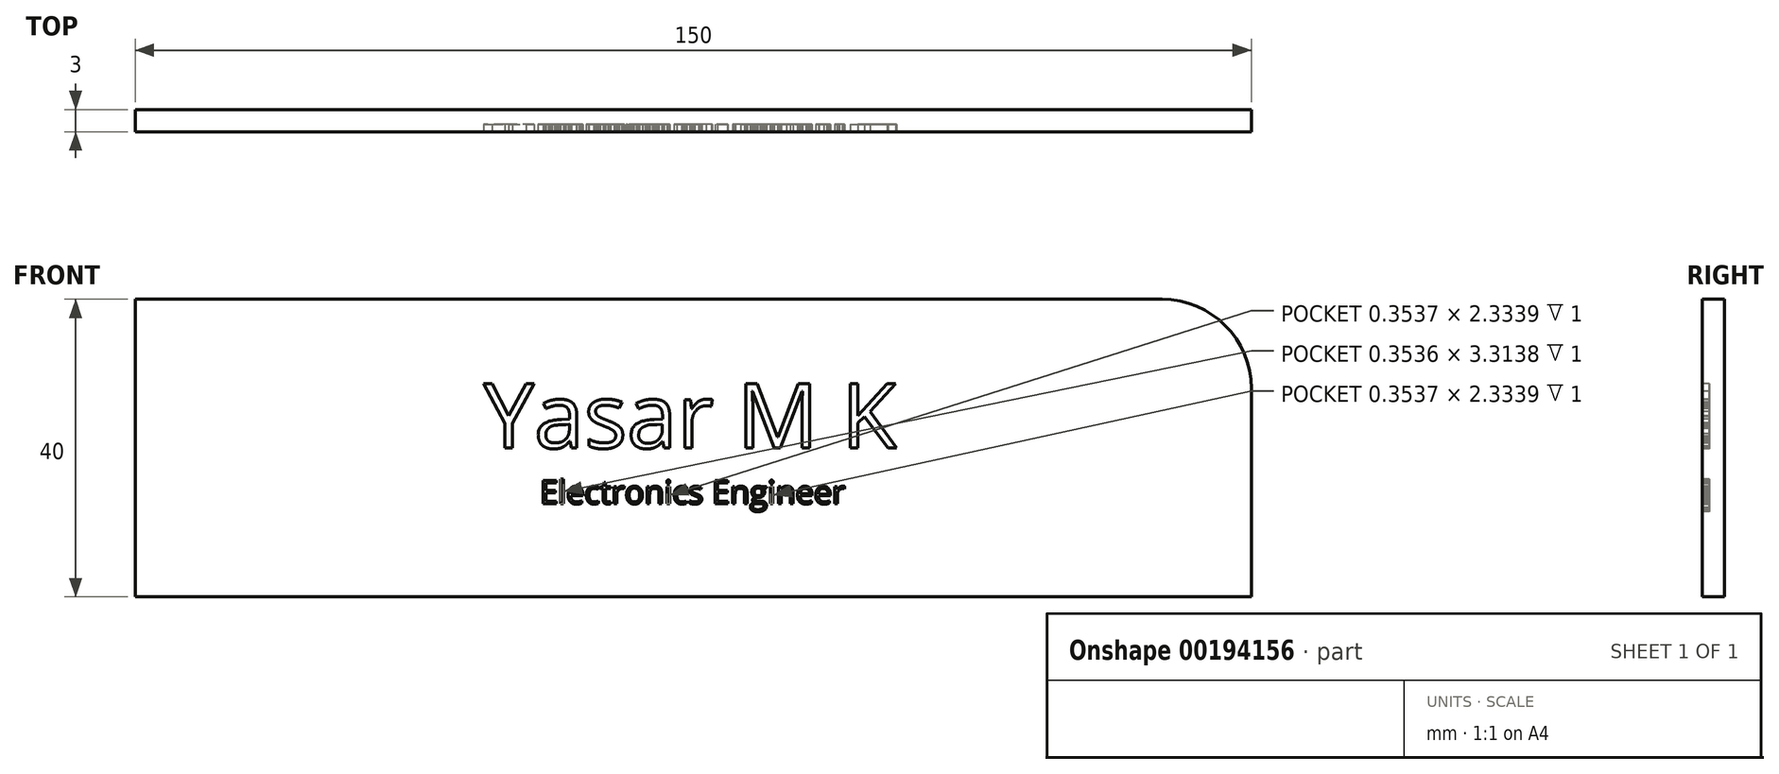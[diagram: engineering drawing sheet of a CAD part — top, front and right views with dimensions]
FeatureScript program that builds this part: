
annotation { "Feature Type Name" : "Feature", "Feature Type Description" : "" }
export const myFeature = defineFeature(function(context is Context, id is Id, definition is map)
    precondition{}
    {
        {
            var Q0;
            Q0=qCreatedBy(makeId("Front.planeOp"),FACE);
            var sketch = newSketch(context, id + "F0", { "sketchPlane" : qUnion([Q0])});
            skLineSegment(sketch, "E0.bottom", {"start": v(-75, 20) * mm, "end": v(63, 20) * mm});
            skLineSegment(sketch, "E0.left", {"start": v(-75, 20) * mm, "end": v(-75, -20) * mm});
            skLineSegment(sketch, "E0.right", {"start": v(75, 8) * mm, "end": v(75, -20) * mm});
            skPoint(sketch, "E1.visualSharp", {"position": v(75, 20) * mm});
            skArc(sketch, "E1.filletArc", {"start": v(75, 8) * mm, "mid": v(71.49, 16.49) * mm, "end": v(63, 20) * mm});
            skLineSegment(sketch, "E2", {"start": v(-75, -20) * mm, "end": v(75, -20) * mm});
            skSolve(sketch);
        }
        {
            var Q0;
            Q0=makeQuery(id+"F0.imprint","IMPRINT",FACE,{"disambiguationData":[TD([[makeQuery(id+"F0.imprint","IMPRINT",EDGE,{"derivedFrom":sQuery(id+"F0.wireOp",EDGE,"E0.bottom")}),-1.0]])]});
            extrude(context, id + "F1", {"entities" : qUnion([Q0]), "depth" : 3 * mm});
        }
        {
            var Q0;
            Q0=makeQuery(id+"F1.opExtrude","CAP_FACE",FACE,{"disambiguationData":[OSD([sQuery(id+"F0.wireOp",EDGE,"E0.bottom"),sQuery(id+"F0.wireOp",EDGE,"E0.left"),sQuery(id+"F0.wireOp",EDGE,"E0.right"),sQuery(id+"F0.wireOp",EDGE,"E1.filletArc"),sQuery(id+"F0.wireOp",EDGE,"E2")])],"isStart":false});
            var sketch = newSketch(context, id + "F2", { "sketchPlane" : qUnion([Q0])});
            skText(sketch, "E3", { "text": "Yasar M K", "fontName": "OpenSans-Regular.ttf"});
            skText(sketch, "E4", { "text": "Electronics Engineer", "fontName": "OpenSans-Regular.ttf"});
            skArc(sketch, "E5", {"start": v(-16.98, 1.48) * mm, "mid": v(-16.69, 2.35) * mm, "end": v(-16.68, 3.27) * mm});
            skArc(sketch, "E6", {"start": v(-17.87, 0.77) * mm, "mid": v(-17.35, 1.03) * mm, "end": v(-16.98, 1.48) * mm});
            skArc(sketch, "E7", {"start": v(-19.24, 0.77) * mm, "mid": v(-18.55, 0.7) * mm, "end": v(-17.87, 0.77) * mm});
            skArc(sketch, "E8", {"start": v(-19.77, 2.04) * mm, "mid": v(-19.72, 1.32) * mm, "end": v(-19.24, 0.77) * mm});
            skArc(sketch, "E9", {"start": v(-18.94, 2.96) * mm, "mid": v(-19.49, 2.62) * mm, "end": v(-19.77, 2.04) * mm});
            skArc(sketch, "E10", {"start": v(-18.06, 3.07) * mm, "mid": v(-18.5, 3.08) * mm, "end": v(-18.94, 2.96) * mm});
            skLineSegment(sketch, "E11", {"start": v(-18.06, 3.07) * mm, "end": v(-16.67, 3.2) * mm});
            skArc(sketch, "E12", {"start": v(-4.51, 1.44) * mm, "mid": v(-4.22, 2.3) * mm, "end": v(-4.22, 3.22) * mm});
            skArc(sketch, "E13", {"start": v(-5.4, 0.73) * mm, "mid": v(-4.88, 0.98) * mm, "end": v(-4.51, 1.44) * mm});
            skArc(sketch, "E14", {"start": v(-6.77, 0.73) * mm, "mid": v(-6.09, 0.66) * mm, "end": v(-5.4, 0.73) * mm});
            skArc(sketch, "E15", {"start": v(-7.3, 2) * mm, "mid": v(-7.26, 1.27) * mm, "end": v(-6.77, 0.73) * mm});
            skArc(sketch, "E16", {"start": v(-6.47, 2.92) * mm, "mid": v(-7.03, 2.58) * mm, "end": v(-7.3, 2) * mm});
            skArc(sketch, "E17", {"start": v(-5.5, 3.14) * mm, "mid": v(-6, 3.11) * mm, "end": v(-6.47, 2.92) * mm});
            skLineSegment(sketch, "E18", {"start": v(-5.5, 3.14) * mm, "end": v(-4.2, 3.16) * mm});
            skLineSegment(sketch, "E19", {"start": v(-16.43, -6.1) * mm, "end": v(-15.21, -6.1) * mm});
            skArc(sketch, "E20", {"start": v(-15.21, -6.1) * mm, "mid": v(-15.82, -5.42) * mm, "end": v(-16.43, -6.1) * mm});
            skLineSegment(sketch, "E21", {"start": v(14.42, -6.12) * mm, "end": v(15.64, -6.12) * mm});
            skArc(sketch, "E22", {"start": v(15.64, -6.12) * mm, "mid": v(15.03, -5.43) * mm, "end": v(14.42, -6.12) * mm});
            skLineSegment(sketch, "E23", {"start": v(16.92, -6.23) * mm, "end": v(18.14, -6.23) * mm});
            skArc(sketch, "E24", {"start": v(18.14, -6.23) * mm, "mid": v(17.53, -5.53) * mm, "end": v(16.92, -6.23) * mm});
            skEllipse(sketch, "E25", {"center": v(-7.9, -6.3) * mm, "majorRadius": 0.91 * mm, "minorRadius": 0.7 * mm, "majorAxis": v(0, -1)});
            const initialGuessF2  = {"E3": [-0.02816, 0, 1, 0, 0.0087], "E4": [-0.02059, -0.0075, 1, 0, 0.00314]};
            skSetInitialGuess(sketch, initialGuessF2);
            skSolve(sketch);
        }
        {
            var Q0;
            Q0 = qSketchRegion(id + "F2", true);
            extrude(context, id + "F3", {"entities" : qUnion([Q0]), "operationType" : NewBodyOperationType.REMOVE, "oppositeDirection" : true, "depth" : 1 * mm});
        }
        {
            var Q0;
            Q0=makeQuery(id+"F0.imprint","IMPRINT",FACE,{"disambiguationData":[TD([[makeQuery(id+"F0.imprint","IMPRINT",EDGE,{"derivedFrom":sQuery(id+"F0.wireOp",EDGE,"E0.bottom")}),-1.0]])]});
            extrude(context, id + "F4", {"entities" : qUnion([Q0]), "operationType" : NewBodyOperationType.REMOVE, "oppositeDirection" : true, "depth" : 2 * mm});
        }
    });
